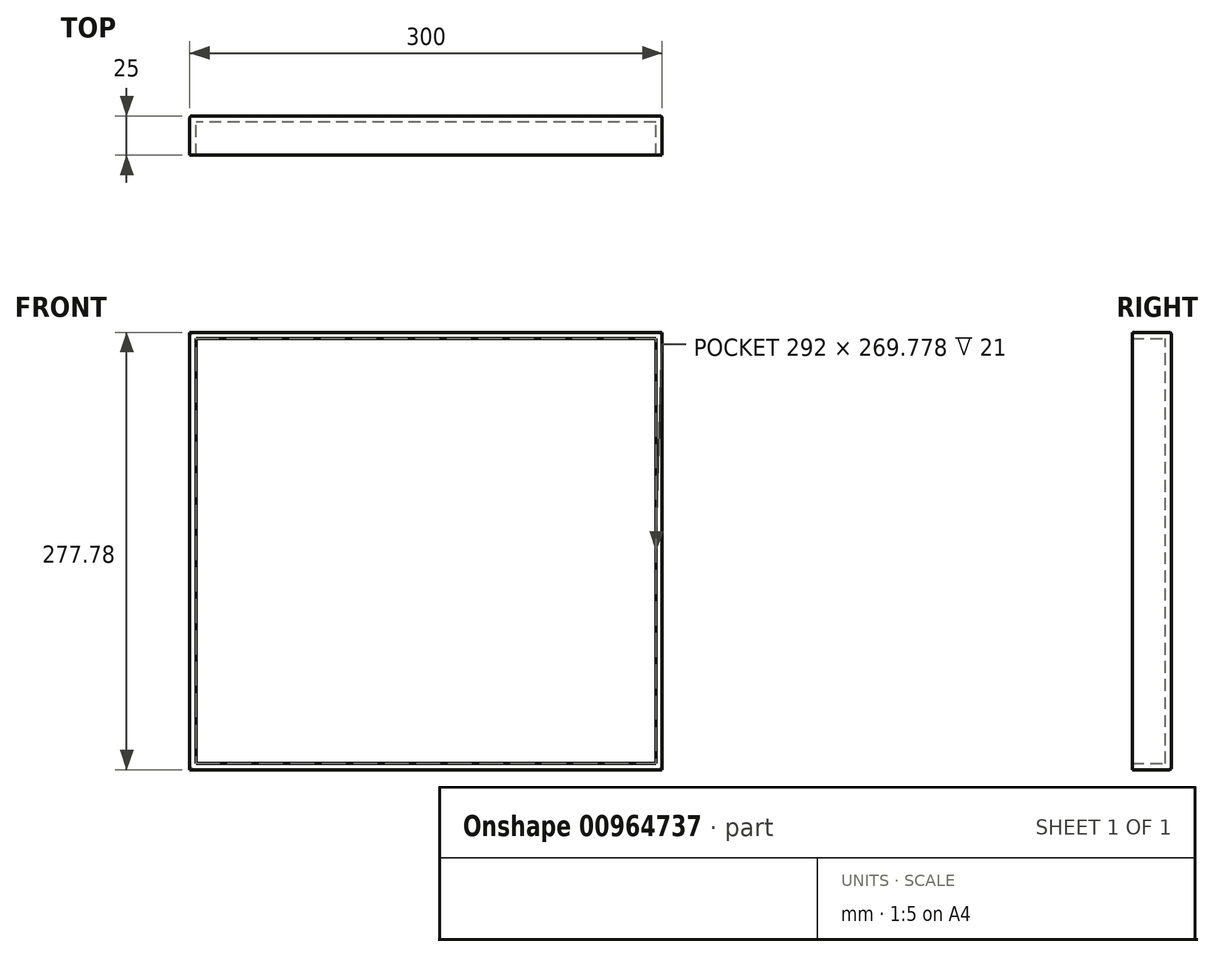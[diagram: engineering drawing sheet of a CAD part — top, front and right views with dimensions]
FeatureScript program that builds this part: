
annotation { "Feature Type Name" : "Feature", "Feature Type Description" : "" }
export const myFeature = defineFeature(function(context is Context, id is Id, definition is map)
    precondition{}
    {
        {
            var Q0;
            Q0=qCreatedBy(makeId("Front.planeOp"),FACE);
            var sketch = newSketch(context, id + "F0", { "sketchPlane" : qUnion([Q0])});
            skLineSegment(sketch, "E0.bottom", {"start": v(150, -138.89) * mm, "end": v(-150, -138.89) * mm});
            skLineSegment(sketch, "E0.top", {"start": v(150, 138.89) * mm, "end": v(-150, 138.89) * mm});
            skLineSegment(sketch, "E0.left", {"start": v(150, -138.89) * mm, "end": v(150, 138.89) * mm});
            skLineSegment(sketch, "E0.right", {"start": v(-150, -138.89) * mm, "end": v(-150, 138.89) * mm});
            skPoint(sketch, "E0.middle", {"position": v(0, 0) * mm});
            skSolve(sketch);
        }
        {
            var Q0;
            Q0=makeQuery(id+"F0.imprint","IMPRINT",FACE,{"disambiguationData":[TD([[makeQuery(id+"F0.imprint","IMPRINT",EDGE,{"derivedFrom":sQuery(id+"F0.wireOp",EDGE,"E0.bottom")}),-1.0]])]});
            extrude(context, id + "F1", {"entities" : qUnion([Q0]), "depth" : 25 * mm, "offsetDistance" : 25 * mm});
        }
        {
            var Q0;
            Q0=makeQuery(id+"F1.opExtrude","CAP_FACE",FACE,{"disambiguationData":[OSD([sQuery(id+"F0.wireOp",EDGE,"E0.bottom"),sQuery(id+"F0.wireOp",EDGE,"E0.top"),sQuery(id+"F0.wireOp",EDGE,"E0.left"),sQuery(id+"F0.wireOp",EDGE,"E0.right")])],"isStart":false});
            shell(context, id + "F2", {"entities" : qUnion([Q0]), "thickness" : 4 * mm});
        }
        {
            var Q0;
            Q0=makeQuery(id+"F1.opExtrude","CAP_FACE",FACE,{"disambiguationData":[OSD([sQuery(id+"F0.wireOp",EDGE,"E0.bottom"),sQuery(id+"F0.wireOp",EDGE,"E0.top"),sQuery(id+"F0.wireOp",EDGE,"E0.left"),sQuery(id+"F0.wireOp",EDGE,"E0.right")])],"isStart":true});
            var Q1;
            Q1=makeQuery(id+"F1.opExtrude","CAP_EDGE",EDGE,{"disambiguationData":[OSD([sQuery(id+"F0.wireOp",EDGE,"E0.right")])],"isStart":true});
            fillet(context, id + "F3", {"entities" : qUnion([Q0, Q1]), "radius" : 1.5 * mm, "tangentPropagation" : true, "allowEdgeOverflow" : false});
        }
    });
